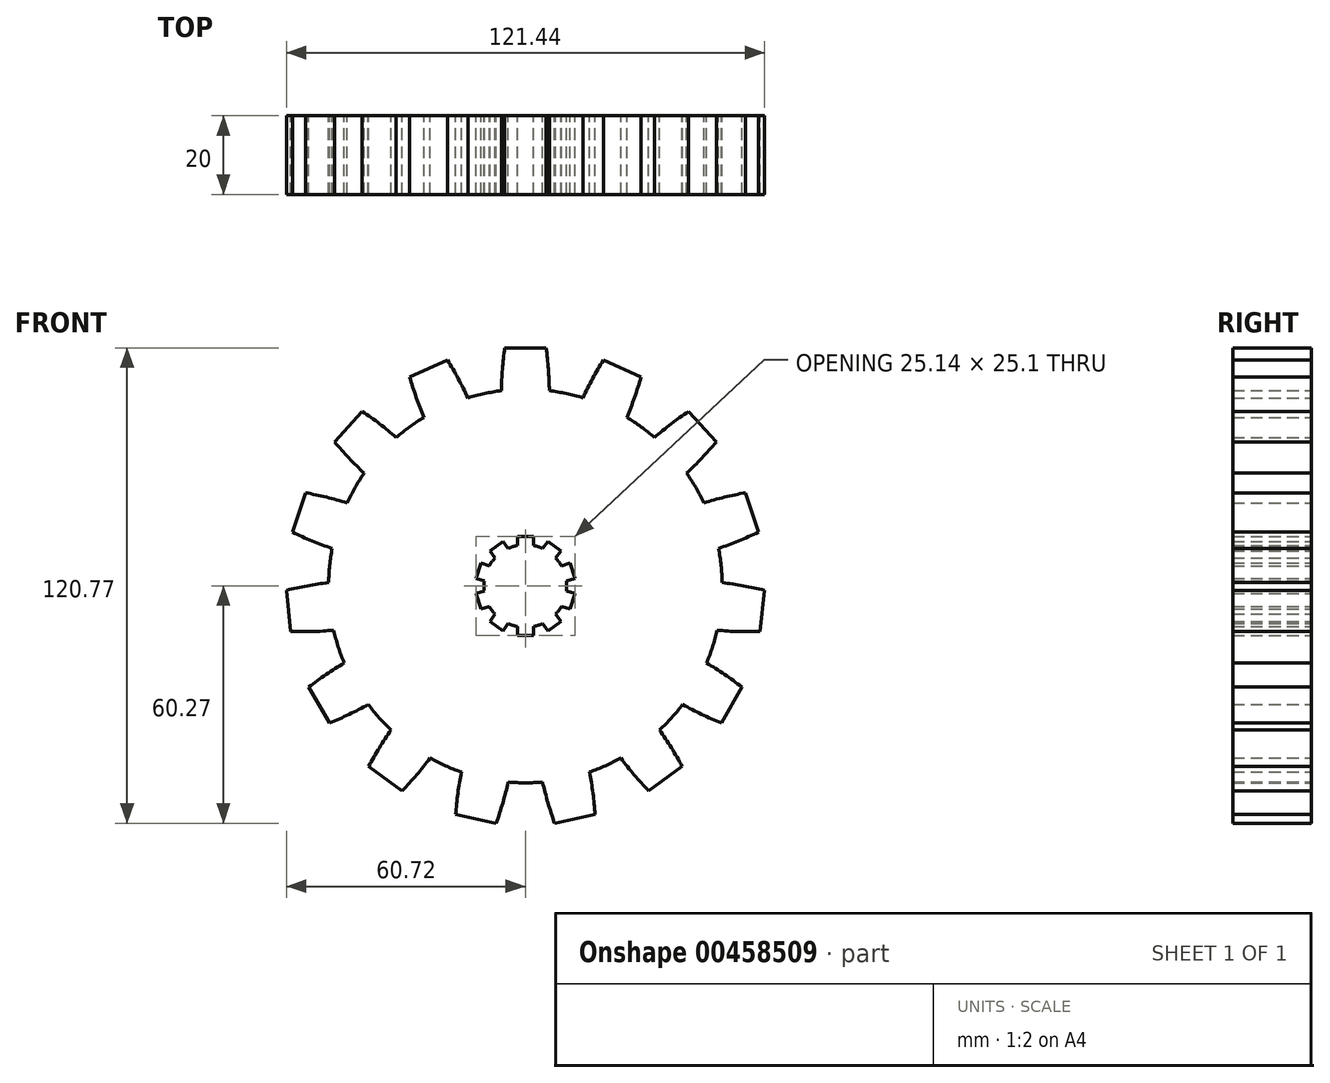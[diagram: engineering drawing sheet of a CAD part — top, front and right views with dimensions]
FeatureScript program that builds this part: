
annotation { "Feature Type Name" : "Feature", "Feature Type Description" : "" }
export const myFeature = defineFeature(function(context is Context, id is Id, definition is map)
    precondition{}
    {
        {
            var Q0;
            Q0=qCreatedBy(makeId("Front.planeOp"),FACE);
            var sketch = newSketch(context, id + "F0", { "sketchPlane" : qUnion([Q0])});
            skArc(sketch, "E0", {"start": v(-40.96, 28.68) * mm, "mid": v(-43.3, 25) * mm, "end": v(-45.32, 21.13) * mm});
            skArc(sketch, "E1", {"start": v(-4.4, -9.54) * mm, "mid": v(-3.24, -9.99) * mm, "end": v(-2.05, -10.3) * mm});
            skLineSegment(sketch, "E2.bottom", {"start": v(-2.05, 12.55) * mm, "end": v(2.05, 12.55) * mm});
            skLineSegment(sketch, "E2.top", {"start": v(-2.05, -12.55) * mm, "end": v(2.05, -12.55) * mm});
            skLineSegment(sketch, "E2.left", {"start": v(-2.05, 12.55) * mm, "end": v(-2.05, 10.3) * mm});
            skLineSegment(sketch, "E2.right", {"start": v(2.05, 12.55) * mm, "end": v(2.05, 10.3) * mm});
            skLineSegment(sketch, "E3.1.0", {"start": v(-5.72, 11.36) * mm, "end": v(-4.4, 9.54) * mm});
            skLineSegment(sketch, "E3.1.1", {"start": v(-9.04, 8.95) * mm, "end": v(-7.71, 7.13) * mm});
            skLineSegment(sketch, "E3.1.2", {"start": v(-9.04, 8.95) * mm, "end": v(-5.72, 11.36) * mm});
            skLineSegment(sketch, "E3.1.3", {"start": v(5.72, -11.36) * mm, "end": v(9.04, -8.95) * mm});
            skLineSegment(sketch, "E3.2.0", {"start": v(-11.3, 5.83) * mm, "end": v(-9.16, 5.13) * mm});
            skLineSegment(sketch, "E3.2.1", {"start": v(-12.57, 1.93) * mm, "end": v(-10.43, 1.23) * mm});
            skLineSegment(sketch, "E3.2.2", {"start": v(-12.57, 1.93) * mm, "end": v(-11.3, 5.83) * mm});
            skLineSegment(sketch, "E3.2.3", {"start": v(11.3, -5.83) * mm, "end": v(12.57, -1.93) * mm});
            skLineSegment(sketch, "E4.3.3.0", {"start": v(-11.3, -5.83) * mm, "end": v(-9.16, -5.13) * mm});
            skLineSegment(sketch, "E4.5.3.0", {"start": v(-12.57, -1.93) * mm, "end": v(-10.43, -1.23) * mm});
            skLineSegment(sketch, "E4.6.3.0", {"start": v(-11.3, -5.83) * mm, "end": v(-12.57, -1.93) * mm});
            skLineSegment(sketch, "E4.9.3.0", {"start": v(12.57, 1.93) * mm, "end": v(11.3, 5.83) * mm});
            skLineSegment(sketch, "E4.3.4.0", {"start": v(-5.72, -11.36) * mm, "end": v(-4.4, -9.54) * mm});
            skLineSegment(sketch, "E4.5.4.0", {"start": v(-9.04, -8.95) * mm, "end": v(-7.71, -7.13) * mm});
            skLineSegment(sketch, "E4.6.4.0", {"start": v(-5.72, -11.36) * mm, "end": v(-9.04, -8.95) * mm});
            skLineSegment(sketch, "E4.9.4.0", {"start": v(9.04, 8.95) * mm, "end": v(5.72, 11.36) * mm});
            skLineSegment(sketch, "E4.3.5.0", {"start": v(2.05, -12.55) * mm, "end": v(2.05, -10.3) * mm});
            skLineSegment(sketch, "E4.6.5.0", {"start": v(2.05, -12.55) * mm, "end": v(-2.05, -12.55) * mm});
            skLineSegment(sketch, "E4.9.5.0", {"start": v(2.05, 12.55) * mm, "end": v(-2.05, 12.55) * mm});
            skLineSegment(sketch, "E4.3.6.0", {"start": v(9.04, -8.95) * mm, "end": v(7.71, -7.13) * mm});
            skLineSegment(sketch, "E4.5.6.0", {"start": v(5.72, -11.36) * mm, "end": v(4.4, -9.54) * mm});
            skLineSegment(sketch, "E4.6.6.0", {"start": v(9.04, -8.95) * mm, "end": v(5.72, -11.36) * mm});
            skLineSegment(sketch, "E4.9.6.0", {"start": v(-5.72, 11.36) * mm, "end": v(-9.04, 8.95) * mm});
            skLineSegment(sketch, "E4.3.7.0", {"start": v(12.57, -1.93) * mm, "end": v(10.43, -1.23) * mm});
            skLineSegment(sketch, "E4.5.7.0", {"start": v(11.3, -5.83) * mm, "end": v(9.16, -5.13) * mm});
            skLineSegment(sketch, "E4.6.7.0", {"start": v(12.57, -1.93) * mm, "end": v(11.3, -5.83) * mm});
            skLineSegment(sketch, "E4.9.7.0", {"start": v(-11.3, 5.83) * mm, "end": v(-12.57, 1.93) * mm});
            skLineSegment(sketch, "E4.3.8.0", {"start": v(11.3, 5.83) * mm, "end": v(9.16, 5.13) * mm});
            skLineSegment(sketch, "E4.5.8.0", {"start": v(12.57, 1.93) * mm, "end": v(10.43, 1.23) * mm});
            skLineSegment(sketch, "E4.6.8.0", {"start": v(11.3, 5.83) * mm, "end": v(12.57, 1.93) * mm});
            skLineSegment(sketch, "E4.9.8.0", {"start": v(-12.57, -1.93) * mm, "end": v(-11.3, -5.83) * mm});
            skLineSegment(sketch, "E4.3.9.0", {"start": v(5.72, 11.36) * mm, "end": v(4.4, 9.54) * mm});
            skLineSegment(sketch, "E4.5.9.0", {"start": v(9.04, 8.95) * mm, "end": v(7.71, 7.13) * mm});
            skLineSegment(sketch, "E4.6.9.0", {"start": v(5.72, 11.36) * mm, "end": v(9.04, 8.95) * mm});
            skLineSegment(sketch, "E4.9.9.0", {"start": v(-9.04, -8.95) * mm, "end": v(-5.72, -11.36) * mm});
            skLineSegment(sketch, "E5.trimOffspring", {"start": v(-2.05, 10.3) * mm, "end": v(-2.05, 12.55) * mm});
            skLineSegment(sketch, "E6.trimOffspring", {"start": v(2.05, 10.3) * mm, "end": v(2.05, 12.55) * mm});
            skLineSegment(sketch, "E7.trimOffspring", {"start": v(4.4, 9.54) * mm, "end": v(5.72, 11.36) * mm});
            skLineSegment(sketch, "E8.trimOffspring", {"start": v(7.71, 7.13) * mm, "end": v(9.04, 8.95) * mm});
            skLineSegment(sketch, "E9.trimOffspring", {"start": v(9.16, 5.13) * mm, "end": v(11.3, 5.83) * mm});
            skLineSegment(sketch, "E10.trimOffspring", {"start": v(-7.71, 7.13) * mm, "end": v(-9.04, 8.95) * mm});
            skLineSegment(sketch, "E11.trimOffspring", {"start": v(-4.4, 9.54) * mm, "end": v(-5.72, 11.36) * mm});
            skLineSegment(sketch, "E12.trimOffspring", {"start": v(-10.43, -1.23) * mm, "end": v(-12.57, -1.93) * mm});
            skLineSegment(sketch, "E13.trimOffspring", {"start": v(2.05, -10.3) * mm, "end": v(2.05, -12.55) * mm});
            skLineSegment(sketch, "E14.trimOffspring", {"start": v(-2.05, -10.3) * mm, "end": v(-2.05, -12.55) * mm});
            skLineSegment(sketch, "E15.trimOffspring", {"start": v(4.4, -9.54) * mm, "end": v(5.72, -11.36) * mm});
            skLineSegment(sketch, "E16.trimOffspring", {"start": v(-9.16, -5.13) * mm, "end": v(-11.3, -5.83) * mm});
            skLineSegment(sketch, "E17.trimOffspring", {"start": v(-7.71, -7.13) * mm, "end": v(-9.04, -8.95) * mm});
            skLineSegment(sketch, "E18.trimOffspring", {"start": v(-10.43, 1.23) * mm, "end": v(-12.57, 1.93) * mm});
            skLineSegment(sketch, "E19.trimOffspring", {"start": v(-9.16, 5.13) * mm, "end": v(-11.3, 5.83) * mm});
            skLineSegment(sketch, "E20.trimOffspring", {"start": v(10.43, -1.23) * mm, "end": v(12.57, -1.93) * mm});
            skLineSegment(sketch, "E21.trimOffspring", {"start": v(10.43, 1.23) * mm, "end": v(12.57, 1.93) * mm});
            skLineSegment(sketch, "E22.trimOffspring", {"start": v(9.16, -5.13) * mm, "end": v(11.3, -5.83) * mm});
            skLineSegment(sketch, "E23.trimOffspring", {"start": v(7.71, -7.13) * mm, "end": v(9.04, -8.95) * mm});
            skLineSegment(sketch, "E24.trimOffspring", {"start": v(-4.4, -9.54) * mm, "end": v(-5.72, -11.36) * mm});
            skArc(sketch, "E25", {"start": v(-5.26, 60.5) * mm, "mid": v(-5.84, 55.08) * mm, "end": v(-6.09, 49.63) * mm});
            skArc(sketch, "E26.MirrorC", {"start": v(5.26, 60.5) * mm, "mid": v(5.84, 55.08) * mm, "end": v(6.09, 49.63) * mm});
            skLineSegment(sketch, "E27", {"start": v(-5.26, 60.5) * mm, "end": v(5.26, 60.5) * mm});
            skPoint(sketch, "E28", {"position": v(0, 60.5) * mm});
            skArc(sketch, "E29.1.0", {"start": v(-19.8, 57.4) * mm, "mid": v(-17.07, 52.7) * mm, "end": v(-14.62, 47.81) * mm});
            skArc(sketch, "E29.1.1", {"start": v(-29.42, 53.13) * mm, "mid": v(-27.74, 47.94) * mm, "end": v(-25.75, 42.86) * mm});
            skLineSegment(sketch, "E29.1.2", {"start": v(-29.42, 53.13) * mm, "end": v(-19.8, 57.4) * mm});
            skArc(sketch, "E29.2.0", {"start": v(-41.44, 44.4) * mm, "mid": v(-37.02, 41.2) * mm, "end": v(-32.8, 37.73) * mm});
            skArc(sketch, "E29.2.1", {"start": v(-48.48, 36.57) * mm, "mid": v(-44.84, 32.51) * mm, "end": v(-40.96, 28.68) * mm});
            skLineSegment(sketch, "E29.2.2", {"start": v(-48.48, 36.57) * mm, "end": v(-41.44, 44.4) * mm});
            skArc(sketch, "E29.3.0", {"start": v(-55.91, 23.7) * mm, "mid": v(-50.58, 22.57) * mm, "end": v(-45.32, 21.13) * mm});
            skArc(sketch, "E29.3.1", {"start": v(-59.17, 13.7) * mm, "mid": v(-54.19, 11.46) * mm, "end": v(-49.08, 9.54) * mm});
            skLineSegment(sketch, "E29.3.2", {"start": v(-59.17, 13.7) * mm, "end": v(-55.91, 23.7) * mm});
            skArc(sketch, "E29.4.0", {"start": v(-60.72, -1.1) * mm, "mid": v(-55.39, 0.05) * mm, "end": v(-50, 0.87) * mm});
            skArc(sketch, "E29.4.1", {"start": v(-59.62, -11.56) * mm, "mid": v(-54.16, -11.57) * mm, "end": v(-48.72, -11.24) * mm});
            skLineSegment(sketch, "E29.4.2", {"start": v(-59.62, -11.56) * mm, "end": v(-60.72, -1.1) * mm});
            skArc(sketch, "E29.5.0", {"start": v(-55.03, -25.7) * mm, "mid": v(-50.62, -22.48) * mm, "end": v(-46.02, -19.54) * mm});
            skArc(sketch, "E29.5.1", {"start": v(-49.76, -34.8) * mm, "mid": v(-44.78, -32.6) * mm, "end": v(-39.93, -30.09) * mm});
            skLineSegment(sketch, "E29.5.2", {"start": v(-49.76, -34.8) * mm, "end": v(-55.03, -25.7) * mm});
            skArc(sketch, "E29.6.0", {"start": v(-39.82, -45.85) * mm, "mid": v(-37.1, -41.12) * mm, "end": v(-34.1, -36.57) * mm});
            skArc(sketch, "E29.6.1", {"start": v(-31.3, -52.04) * mm, "mid": v(-27.65, -48) * mm, "end": v(-24.24, -43.73) * mm});
            skLineSegment(sketch, "E29.6.2", {"start": v(-31.3, -52.04) * mm, "end": v(-39.82, -45.85) * mm});
            skArc(sketch, "E29.7.0", {"start": v(-17.73, -58.08) * mm, "mid": v(-17.16, -52.66) * mm, "end": v(-16.27, -47.28) * mm});
            skArc(sketch, "E29.7.1", {"start": v(-7.43, -60.27) * mm, "mid": v(-5.74, -55.09) * mm, "end": v(-4.36, -49.8) * mm});
            skLineSegment(sketch, "E29.7.2", {"start": v(-7.43, -60.27) * mm, "end": v(-17.73, -58.08) * mm});
            skArc(sketch, "E29.8.0", {"start": v(7.43, -60.27) * mm, "mid": v(5.74, -55.09) * mm, "end": v(4.36, -49.8) * mm});
            skArc(sketch, "E29.8.1", {"start": v(17.73, -58.08) * mm, "mid": v(17.16, -52.66) * mm, "end": v(16.27, -47.28) * mm});
            skLineSegment(sketch, "E29.8.2", {"start": v(17.73, -58.08) * mm, "end": v(7.43, -60.27) * mm});
            skArc(sketch, "E29.9.0", {"start": v(31.3, -52.04) * mm, "mid": v(27.65, -48) * mm, "end": v(24.24, -43.73) * mm});
            skArc(sketch, "E29.9.1", {"start": v(39.82, -45.85) * mm, "mid": v(37.1, -41.12) * mm, "end": v(34.1, -36.57) * mm});
            skLineSegment(sketch, "E29.9.2", {"start": v(39.82, -45.85) * mm, "end": v(31.3, -52.04) * mm});
            skArc(sketch, "E29.10.0", {"start": v(49.76, -34.8) * mm, "mid": v(44.78, -32.6) * mm, "end": v(39.93, -30.09) * mm});
            skArc(sketch, "E29.10.1", {"start": v(55.03, -25.7) * mm, "mid": v(50.62, -22.48) * mm, "end": v(46.02, -19.54) * mm});
            skLineSegment(sketch, "E29.10.2", {"start": v(55.03, -25.7) * mm, "end": v(49.76, -34.8) * mm});
            skArc(sketch, "E29.11.0", {"start": v(59.62, -11.56) * mm, "mid": v(54.16, -11.57) * mm, "end": v(48.72, -11.24) * mm});
            skArc(sketch, "E29.11.1", {"start": v(60.72, -1.1) * mm, "mid": v(55.39, 0.05) * mm, "end": v(50, 0.87) * mm});
            skLineSegment(sketch, "E29.11.2", {"start": v(60.72, -1.1) * mm, "end": v(59.62, -11.56) * mm});
            skArc(sketch, "E29.12.0", {"start": v(59.17, 13.7) * mm, "mid": v(54.19, 11.46) * mm, "end": v(49.08, 9.54) * mm});
            skArc(sketch, "E29.12.1", {"start": v(55.91, 23.7) * mm, "mid": v(50.58, 22.57) * mm, "end": v(45.32, 21.13) * mm});
            skLineSegment(sketch, "E29.12.2", {"start": v(55.91, 23.7) * mm, "end": v(59.17, 13.7) * mm});
            skArc(sketch, "E29.13.0", {"start": v(48.48, 36.57) * mm, "mid": v(44.84, 32.51) * mm, "end": v(40.96, 28.68) * mm});
            skArc(sketch, "E29.13.1", {"start": v(41.44, 44.4) * mm, "mid": v(37.02, 41.2) * mm, "end": v(32.8, 37.73) * mm});
            skLineSegment(sketch, "E29.13.2", {"start": v(41.44, 44.4) * mm, "end": v(48.48, 36.57) * mm});
            skArc(sketch, "E29.14.0", {"start": v(29.42, 53.13) * mm, "mid": v(27.74, 47.94) * mm, "end": v(25.75, 42.86) * mm});
            skArc(sketch, "E29.14.1", {"start": v(19.8, 57.4) * mm, "mid": v(17.07, 52.7) * mm, "end": v(14.62, 47.81) * mm});
            skLineSegment(sketch, "E29.14.2", {"start": v(19.8, 57.4) * mm, "end": v(29.42, 53.13) * mm});
            skArc(sketch, "E30.trimOffspring", {"start": v(-25.75, 42.86) * mm, "mid": v(-29.39, 40.45) * mm, "end": v(-32.8, 37.73) * mm});
            skArc(sketch, "E31.trimOffspring", {"start": v(-6.09, 49.63) * mm, "mid": v(-10.4, 48.9) * mm, "end": v(-14.62, 47.81) * mm});
            skArc(sketch, "E32.trimOffspring", {"start": v(14.62, 47.81) * mm, "mid": v(10.4, 48.9) * mm, "end": v(6.09, 49.63) * mm});
            skArc(sketch, "E33.trimOffspring", {"start": v(32.8, 37.73) * mm, "mid": v(29.39, 40.45) * mm, "end": v(25.75, 42.86) * mm});
            skArc(sketch, "E34.trimOffspring", {"start": v(45.32, 21.13) * mm, "mid": v(43.3, 25) * mm, "end": v(40.96, 28.68) * mm});
            skArc(sketch, "E35.trimOffspring", {"start": v(50, 0.87) * mm, "mid": v(49.73, 5.23) * mm, "end": v(49.08, 9.54) * mm});
            skArc(sketch, "E36.trimOffspring", {"start": v(46.02, -19.54) * mm, "mid": v(47.55, -15.45) * mm, "end": v(48.72, -11.24) * mm});
            skArc(sketch, "E37.trimOffspring", {"start": v(34.1, -36.57) * mm, "mid": v(37.16, -33.46) * mm, "end": v(39.93, -30.09) * mm});
            skArc(sketch, "E38.trimOffspring", {"start": v(16.27, -47.28) * mm, "mid": v(20.34, -45.68) * mm, "end": v(24.24, -43.73) * mm});
            skArc(sketch, "E39.trimOffspring", {"start": v(-4.36, -49.8) * mm, "mid": v(0, -50) * mm, "end": v(4.36, -49.8) * mm});
            skArc(sketch, "E40.trimOffspring", {"start": v(-24.24, -43.73) * mm, "mid": v(-20.34, -45.68) * mm, "end": v(-16.27, -47.28) * mm});
            skArc(sketch, "E41.trimOffspring", {"start": v(-39.93, -30.09) * mm, "mid": v(-37.16, -33.46) * mm, "end": v(-34.1, -36.57) * mm});
            skArc(sketch, "E42.trimOffspring", {"start": v(-48.72, -11.24) * mm, "mid": v(-47.55, -15.45) * mm, "end": v(-46.02, -19.54) * mm});
            skArc(sketch, "E43.trimOffspring", {"start": v(-49.08, 9.54) * mm, "mid": v(-49.73, 5.23) * mm, "end": v(-50, 0.87) * mm});
            skArc(sketch, "E44.trimOffspring", {"start": v(-9.16, -5.13) * mm, "mid": v(-8.5, -6.17) * mm, "end": v(-7.71, -7.13) * mm});
            skArc(sketch, "E45.trimOffspring", {"start": v(-10.43, 1.23) * mm, "mid": v(-10.5, 0) * mm, "end": v(-10.43, -1.23) * mm});
            skArc(sketch, "E46.trimOffspring", {"start": v(-7.71, 7.13) * mm, "mid": v(-8.5, 6.17) * mm, "end": v(-9.16, 5.13) * mm});
            skArc(sketch, "E47.trimOffspring", {"start": v(-2.05, 10.3) * mm, "mid": v(-3.24, 9.99) * mm, "end": v(-4.4, 9.54) * mm});
            skArc(sketch, "E48.trimOffspring", {"start": v(4.4, 9.54) * mm, "mid": v(3.24, 9.99) * mm, "end": v(2.05, 10.3) * mm});
            skArc(sketch, "E49.trimOffspring", {"start": v(9.16, 5.13) * mm, "mid": v(8.5, 6.17) * mm, "end": v(7.71, 7.13) * mm});
            skArc(sketch, "E50.trimOffspring", {"start": v(10.43, -1.23) * mm, "mid": v(10.5, 0) * mm, "end": v(10.43, 1.23) * mm});
            skArc(sketch, "E51.trimOffspring", {"start": v(2.05, -10.3) * mm, "mid": v(3.24, -9.99) * mm, "end": v(4.4, -9.54) * mm});
            skArc(sketch, "E52.trimOffspring", {"start": v(7.71, -7.13) * mm, "mid": v(8.5, -6.17) * mm, "end": v(9.16, -5.13) * mm});
            skSolve(sketch);
        }
        {
            var Q0;
            Q0=makeQuery(id+"F0.imprint","IMPRINT",FACE,{"disambiguationData":[TD([[makeQuery(id+"F0.imprint","IMPRINT",EDGE,{"derivedFrom":sQuery(id+"F0.wireOp",EDGE,"E0")}),1.0]])]});
            extrude(context, id + "F1", {"entities" : qUnion([Q0]), "depth" : 20 * mm});
        }
    });
